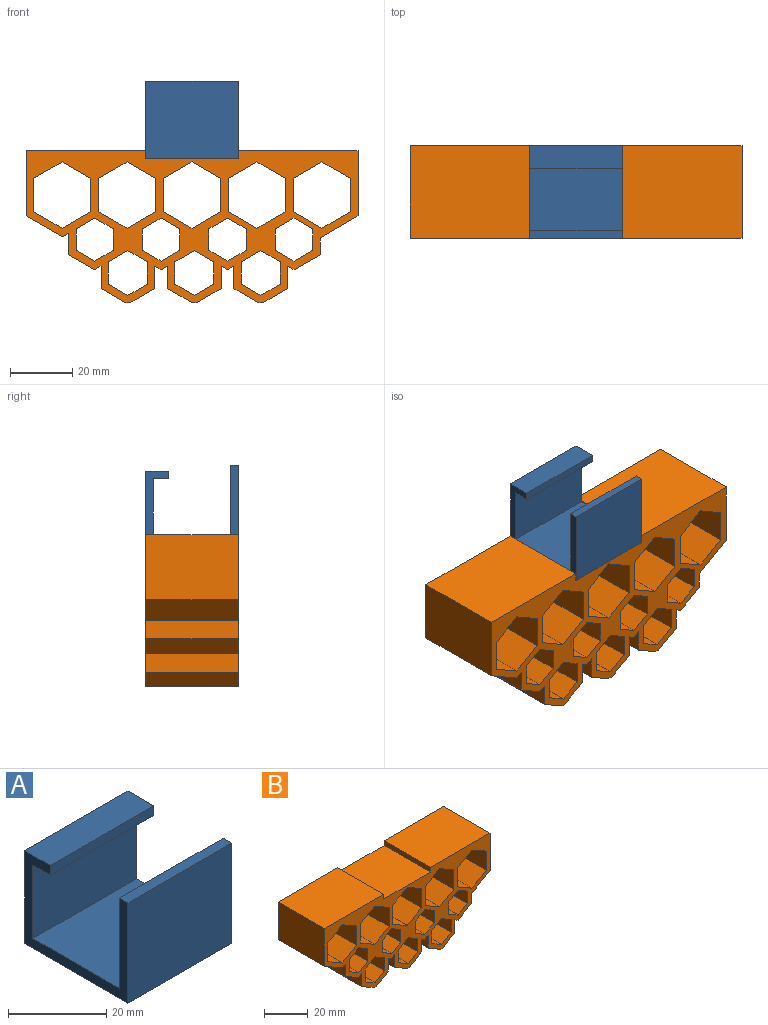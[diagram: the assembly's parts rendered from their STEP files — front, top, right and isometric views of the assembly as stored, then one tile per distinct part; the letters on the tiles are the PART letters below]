
ASSEMBLY  parts=2 mates=1
PART A: 12 faces, bbox 29.8x29.8x25 mm
  f0: plane 29.8x7.4mm, normal (0,0,1), area 220.5mm2, adj f1,f9,f10,f11
  f1: plane 29.8x2.4mm, normal (0,-1,0), area 71.5mm2, adj f0,f2,f10,f11
  f2: plane 29.8x5mm, normal (0,0,-1), area 149mm2, adj f1,f3,f10,f11
  f3: plane 29.8x18.3mm, normal (0,-1,0), area 545.3mm2, adj f2,f4,f10,f11
  f4: plane 29.8x25mm, normal (0,0,1), area 745mm2, adj f3,f5,f10,f11
  f5: plane 29.8x22.6mm, normal (0,1,0), area 673.5mm2, adj f4,f6,f10,f11
  f6: plane 29.8x2.4mm, normal (0,0,1), area 71.5mm2, adj f5,f7,f10,f11
  f7: plane 29.8x25mm, normal (0,-1,0), area 745mm2, adj f6,f8,f10,f11
  f8: plane 29.8x29.8mm, normal (0,0,-1), area 888mm2, adj f7,f9,f10,f11
  f9: plane 29.8x23.1mm, normal (0,1,0), area 688.4mm2, adj f0,f8,f10,f11
  f10: plane 29.8x25mm, normal (1,0,0), area 187.4mm2, adj f0,f1,f2,f3,f4,f5,f6,f7
  f11: plane 29.8x25mm, normal (-1,0,0), area 187.4mm2, adj f0,f1,f2,f3,f4,f5,f6,f7
PART B: 109 faces, bbox 106.9x29.8x49 mm
  f0: plane 106.9x48.98mm, normal (0,1,0), area 1672.6mm2, adj f1,f2,f3,f4,f6,f7,f8,f9
  f1: plane 29.8x1.29mm, normal (0,0,-1), area 38.3mm2, adj f0,f5,f89,f103
  f2: plane 29.8x1.29mm, normal (0,0,-1), area 38.3mm2, adj f0,f5,f95,f101
  f3: plane 29.8x1.29mm, normal (0,0,-1), area 38.3mm2, adj f0,f5,f88,f94
  f4: plane 29.8x21.01mm, normal (1,0,0), area 626mm2, adj f0,f5,f7,f100
  f5: plane 106.9x48.98mm, normal (0,-1,0), area 1672.6mm2, adj f1,f2,f3,f4,f6,f7,f8,f9
  f6: plane 38.45x29.8mm, normal (0,0,1), area 1145.8mm2, adj f0,f5,f8,f83
  f7: plane 38.45x29.8mm, normal (0,0,1), area 1145.8mm2, adj f0,f4,f5,f81
  f8: plane 29.8x21.01mm, normal (-1,0,0), area 626mm2, adj f0,f5,f6,f102
  f9: plane 29.8x10.68mm, normal (-1,0,0), area 318.3mm2, adj f0,f5,f10,f69
  f10: plane 29.8x9.25mm, normal (-0.5,0,0.87), area 318.3mm2, adj f0,f5,f9,f11
  f11: plane 29.8x9.25mm, normal (0.5,0,0.87), area 318.3mm2, adj f0,f5,f10,f12
  f12: plane 29.8x10.68mm, normal (1,0,0), area 318.3mm2, adj f0,f5,f11,f13
  f13: plane 29.8x9.25mm, normal (0.5,0,-0.87), area 318.3mm2, adj f0,f5,f12,f69
  f14: plane 29.8x10.68mm, normal (-1,0,0), area 318.3mm2, adj f0,f5,f15,f70
  f15: plane 29.8x9.25mm, normal (-0.5,0,0.87), area 318.3mm2, adj f0,f5,f14,f16
  f16: plane 29.8x9.25mm, normal (0.5,0,0.87), area 318.3mm2, adj f0,f5,f15,f17
  f17: plane 29.8x10.68mm, normal (1,0,0), area 318.3mm2, adj f0,f5,f16,f18
  f18: plane 29.8x9.25mm, normal (0.5,0,-0.87), area 318.3mm2, adj f0,f5,f17,f70
  f19: plane 29.8x10.68mm, normal (-1,0,0), area 318.3mm2, adj f0,f5,f20,f71
  f20: plane 29.8x9.25mm, normal (-0.5,0,0.87), area 318.3mm2, adj f0,f5,f19,f21
  f21: plane 29.8x9.25mm, normal (0.5,0,0.87), area 318.3mm2, adj f0,f5,f20,f22
  f22: plane 29.8x10.68mm, normal (1,0,0), area 318.3mm2, adj f0,f5,f21,f23
  f23: plane 29.8x9.25mm, normal (0.5,0,-0.87), area 318.3mm2, adj f0,f5,f22,f71
  f24: plane 29.8x10.68mm, normal (-1,0,0), area 318.3mm2, adj f0,f5,f25,f72
  f25: plane 29.8x9.25mm, normal (-0.5,0,0.87), area 318.3mm2, adj f0,f5,f24,f26
  f26: plane 29.8x9.25mm, normal (0.5,0,0.87), area 318.3mm2, adj f0,f5,f25,f27
  f27: plane 29.8x10.68mm, normal (1,0,0), area 318.3mm2, adj f0,f5,f26,f28
  f28: plane 29.8x9.25mm, normal (0.5,0,-0.87), area 318.3mm2, adj f0,f5,f27,f72
  f29: plane 29.8x10.68mm, normal (-1,0,0), area 318.3mm2, adj f0,f5,f30,f73
  f30: plane 29.8x9.25mm, normal (-0.5,0,0.87), area 318.3mm2, adj f0,f5,f29,f31
  f31: plane 29.8x9.25mm, normal (0.5,0,0.87), area 318.3mm2, adj f0,f5,f30,f32
  f32: plane 29.8x10.68mm, normal (1,0,0), area 318.3mm2, adj f0,f5,f31,f33
  f33: plane 29.8x9.25mm, normal (0.5,0,-0.87), area 318.3mm2, adj f0,f5,f32,f73
  f34: plane 29.8x6.93mm, normal (-1,0,0), area 206.5mm2, adj f0,f5,f35,f74
  f35: plane 29.8x6mm, normal (-0.5,0,0.87), area 206.5mm2, adj f0,f5,f34,f36
  f36: plane 29.8x6mm, normal (0.5,0,0.87), area 206.5mm2, adj f0,f5,f35,f37
  f37: plane 29.8x6.93mm, normal (1,0,0), area 206.5mm2, adj f0,f5,f36,f38
  f38: plane 29.8x6mm, normal (0.5,0,-0.87), area 206.5mm2, adj f0,f5,f37,f74
  f39: plane 29.8x6.93mm, normal (1,0,0), area 206.5mm2, adj f0,f5,f40,f75
  f40: plane 29.8x6mm, normal (0.5,0,-0.87), area 206.5mm2, adj f0,f5,f39,f41
  f41: plane 29.8x6mm, normal (-0.5,0,-0.87), area 206.5mm2, adj f0,f5,f40,f42
  f42: plane 29.8x6.93mm, normal (-1,0,0), area 206.5mm2, adj f0,f5,f41,f43
  f43: plane 29.8x6mm, normal (-0.5,0,0.87), area 206.5mm2, adj f0,f5,f42,f75
  f44: plane 29.8x6.93mm, normal (1,0,0), area 206.5mm2, adj f0,f5,f45,f76
  f45: plane 29.8x6mm, normal (0.5,0,-0.87), area 206.5mm2, adj f0,f5,f44,f46
  f46: plane 29.8x6mm, normal (-0.5,0,-0.87), area 206.5mm2, adj f0,f5,f45,f47
  f47: plane 29.8x6.93mm, normal (-1,0,0), area 206.5mm2, adj f0,f5,f46,f48
  f48: plane 29.8x6mm, normal (-0.5,0,0.87), area 206.5mm2, adj f0,f5,f47,f76
  f49: plane 29.8x6.93mm, normal (1,0,0), area 206.5mm2, adj f0,f5,f50,f77
  f50: plane 29.8x6mm, normal (0.5,0,-0.87), area 206.5mm2, adj f0,f5,f49,f51
  f51: plane 29.8x6mm, normal (-0.5,0,-0.87), area 206.5mm2, adj f0,f5,f50,f52
  f52: plane 29.8x6.93mm, normal (-1,0,0), area 206.5mm2, adj f0,f5,f51,f53
  f53: plane 29.8x6mm, normal (-0.5,0,0.87), area 206.5mm2, adj f0,f5,f52,f77
  f54: plane 29.8x7.22mm, normal (-1,0,0), area 215.1mm2, adj f0,f5,f55,f78
  f55: plane 29.8x6.25mm, normal (-0.5,0,0.87), area 215.1mm2, adj f0,f5,f54,f56
  f56: plane 29.8x6.25mm, normal (0.5,0,0.87), area 215.1mm2, adj f0,f5,f55,f57
  f57: plane 29.8x7.22mm, normal (1,0,0), area 215.1mm2, adj f0,f5,f56,f58
  f58: plane 29.8x6.25mm, normal (0.5,0,-0.87), area 215.1mm2, adj f0,f5,f57,f78
  f59: plane 29.8x6.25mm, normal (0.5,0,0.87), area 215.1mm2, adj f0,f5,f60,f79
  f60: plane 29.8x7.22mm, normal (1,0,0), area 215.1mm2, adj f0,f5,f59,f61
  f61: plane 29.8x6.25mm, normal (0.5,0,-0.87), area 215.1mm2, adj f0,f5,f60,f62
  f62: plane 29.8x6.25mm, normal (-0.5,0,-0.87), area 215.1mm2, adj f0,f5,f61,f63
  f63: plane 29.8x7.22mm, normal (-1,0,0), area 215.1mm2, adj f0,f5,f62,f79
  f64: plane 29.8x6.25mm, normal (0.5,0,0.87), area 215.1mm2, adj f0,f5,f65,f80
  f65: plane 29.8x7.22mm, normal (1,0,0), area 215.1mm2, adj f0,f5,f64,f66
  f66: plane 29.8x6.25mm, normal (0.5,0,-0.87), area 215.1mm2, adj f0,f5,f65,f67
  f67: plane 29.8x6.25mm, normal (-0.5,0,-0.87), area 215.1mm2, adj f0,f5,f66,f68
  f68: plane 29.8x7.22mm, normal (-1,0,0), area 215.1mm2, adj f0,f5,f67,f80
  f69: plane 29.8x9.25mm, normal (-0.5,0,-0.87), area 318.3mm2, adj f0,f5,f9,f13
  f70: plane 29.8x9.25mm, normal (-0.5,0,-0.87), area 318.3mm2, adj f0,f5,f14,f18
  f71: plane 29.8x9.25mm, normal (-0.5,0,-0.87), area 318.3mm2, adj f0,f5,f19,f23
  f72: plane 29.8x9.25mm, normal (-0.5,0,-0.87), area 318.3mm2, adj f0,f5,f24,f28
  f73: plane 29.8x9.25mm, normal (-0.5,0,-0.87), area 318.3mm2, adj f0,f5,f29,f33
  f74: plane 29.8x6mm, normal (-0.5,0,-0.87), area 206.5mm2, adj f0,f5,f34,f38
  f75: plane 29.8x6mm, normal (0.5,0,0.87), area 206.5mm2, adj f0,f5,f39,f43
  f76: plane 29.8x6mm, normal (0.5,0,0.87), area 206.5mm2, adj f0,f5,f44,f48
  f77: plane 29.8x6mm, normal (0.5,0,0.87), area 206.5mm2, adj f0,f5,f49,f53
  f78: plane 29.8x6.25mm, normal (-0.5,0,-0.87), area 215.1mm2, adj f0,f5,f54,f58
  f79: plane 29.8x6.25mm, normal (-0.5,0,0.87), area 215.1mm2, adj f0,f5,f59,f63
  f80: plane 29.8x6.25mm, normal (-0.5,0,0.87), area 215.1mm2, adj f0,f5,f64,f68
  f81: plane 29.8x2.6mm, normal (-1,0,0), area 77.5mm2, adj f0,f5,f7,f82
  f82: plane 30x29.8mm, normal (0,0,1), area 894mm2, adj f0,f5,f81,f83
  f83: plane 29.8x2.6mm, normal (1,0,0), area 77.5mm2, adj f0,f5,f6,f82
  f84: plane 29.8x7.22mm, normal (1,0,0), area 215.1mm2, adj f0,f5,f85,f89
  f85: plane 29.8x2.05mm, normal (-0.5,0,-0.87), area 70.5mm2, adj f0,f5,f84,f86
  f86: plane 29.8x2.05mm, normal (0.5,0,-0.87), area 70.5mm2, adj f0,f5,f85,f87
  f87: plane 29.8x7.22mm, normal (-1,0,0), area 215.1mm2, adj f0,f5,f86,f88
  f88: plane 29.8x8.01mm, normal (-0.5,0,-0.87), area 275.5mm2, adj f0,f3,f5,f87
  f89: plane 29.8x8.01mm, normal (0.5,0,-0.87), area 275.5mm2, adj f0,f1,f5,f84
  f90: plane 29.8x7.22mm, normal (1,0,0), area 215.1mm2, adj f0,f5,f91,f94
  f91: plane 29.8x2.05mm, normal (-0.5,0,-0.87), area 70.5mm2, adj f0,f5,f90,f92
  f92: plane 29.8x2.05mm, normal (0.5,0,-0.87), area 70.5mm2, adj f0,f5,f91,f93
  f93: plane 29.8x7.22mm, normal (-1,0,0), area 215.1mm2, adj f0,f5,f92,f95
  f94: plane 29.8x8.01mm, normal (0.5,0,-0.87), area 275.5mm2, adj f0,f3,f5,f90
  f95: plane 29.8x8.01mm, normal (-0.5,0,-0.87), area 275.5mm2, adj f0,f2,f5,f93
  f96: plane 29.8x7.22mm, normal (1,0,0), area 215.1mm2, adj f0,f5,f97,f101
  f97: plane 29.8x2.05mm, normal (-0.5,0,-0.87), area 70.5mm2, adj f0,f5,f96,f98
  f98: plane 29.8x8.4mm, normal (0.5,0,-0.87), area 289mm2, adj f0,f5,f97,f99
  f99: plane 29.8x5.43mm, normal (1,0,0), area 161.7mm2, adj f0,f5,f98,f100
  f100: plane 29.8x12.2mm, normal (0.5,0,-0.87), area 419.8mm2, adj f0,f4,f5,f99
  f101: plane 29.8x8.01mm, normal (0.5,0,-0.87), area 275.5mm2, adj f0,f2,f5,f96
  f102: plane 29.8x11.65mm, normal (-0.5,0,-0.87), area 400.9mm2, adj f0,f5,f8,f108
  f103: plane 29.8x8.01mm, normal (-0.5,0,-0.87), area 275.5mm2, adj f0,f1,f5,f104
  f104: plane 29.8x7.22mm, normal (-1,0,0), area 215.1mm2, adj f0,f5,f103,f105
  f105: plane 29.8x2.05mm, normal (0.5,0,-0.87), area 70.5mm2, adj f0,f5,f104,f106
  f106: plane 29.8x8.4mm, normal (-0.5,0,-0.87), area 289mm2, adj f0,f5,f105,f107
  f107: plane 29.8x6.93mm, normal (-1,0,0), area 206.5mm2, adj f0,f5,f106,f108
  f108: plane 29.8x2.05mm, normal (0.5,0,-0.87), area 70.5mm2, adj f0,f5,f102,f107
PLACE A t=(10.43,-29.49,-11.82)mm
PLACE B t=(10.43,-14.59,-23.5)mm
MATE fastened A.f8 <-> B.f82  axis (0,0,-1) through (10.43,-29.49,-11.82)mm
